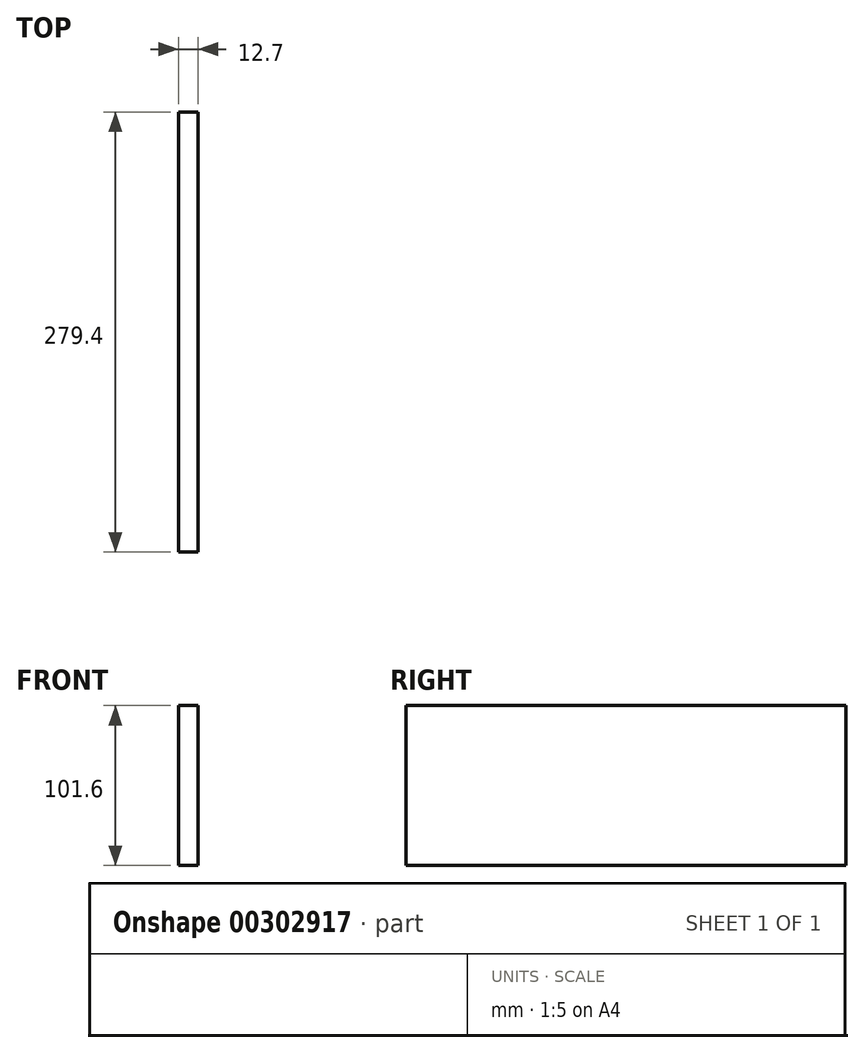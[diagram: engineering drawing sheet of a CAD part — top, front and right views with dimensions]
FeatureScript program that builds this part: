
annotation { "Feature Type Name" : "Feature", "Feature Type Description" : "" }
export const myFeature = defineFeature(function(context is Context, id is Id, definition is map)
    precondition{}
    {
        {
            var Q0;
            Q0=qCreatedBy(makeId("Right.planeOp"),FACE);
            var sketch = newSketch(context, id + "F0", { "sketchPlane" : qUnion([Q0])});
            skLineSegment(sketch, "E0.bottom", {"start": v(139.7, 50.8) * mm, "end": v(-139.7, 50.8) * mm});
            skLineSegment(sketch, "E0.top", {"start": v(139.7, -50.8) * mm, "end": v(-139.7, -50.8) * mm});
            skLineSegment(sketch, "E0.left", {"start": v(139.7, 50.8) * mm, "end": v(139.7, -50.8) * mm});
            skLineSegment(sketch, "E0.right", {"start": v(-139.7, 50.8) * mm, "end": v(-139.7, -50.8) * mm});
            skPoint(sketch, "E0.middle", {"position": v(0, 0) * mm});
            skSolve(sketch);
        }
        {
            var Q0;
            Q0=makeQuery(id+"F0.imprint","IMPRINT",FACE,{"disambiguationData":[TD([[makeQuery(id+"F0.imprint","IMPRINT",EDGE,{"derivedFrom":sQuery(id+"F0.wireOp",EDGE,"E0.bottom")}),1.0]])]});
            extrude(context, id + "F1", {"entities" : qUnion([Q0]), "depth" : 12.7 * mm});
        }
    });
